# Revit family: Lighting-UrbanSystem-GEWISS-URBAN[O3]-LED-SIDE_COUPLING_OPTIC_STREET
name_source: partatom
category: Apparecchi per illuminazione
units: mm (PartAtom-declared; Revit-internal decimal feet)

## family parameters
Condiviso = No
Host = Superficie
Numero OmniClass = 23.80.70.00
Punto di calcolo locali = Sì
Quota connettore circolare = Usa diametro
Sorgente d'illuminazione = No
Taglio con vuoti quando caricato = No
Tipo di parte = Normale
Titolo OmniClass = Lighting

## types (4) — shared parameters
Application = External
Catalogue = LIGHTING
Catalogue Range = URBAN [O3]
Colour = Graphite grey
Colour temperature = 4000 K (CRI 70)
Colour temperature: = 4000 K (CRI 70)
Driver type = Constant Current Driver Led
Electrocod = 244C
Finitura = GEWISS - GRIGIO GRAFITE
IDF = 77868679-f757-4753-85ef-7763ddad7a87
IDT = 85d5c301-9efa-429f-8169-5776374b703b
IP degree = IP66
Immagine tipo = GW87601.jpg
Insulation class = II
LED Life time (L80B10) = 100000H
LED Life time (L90B20) = 50000H
LED LifeTime (L80B20) = 50000H
LED current = 530mA
Maximum surface exposed to the wind = 0,25M2
Minimum distance from the illuminated object = 1M
Operating temperature: = -25 +35 °C
Optic = Street - ULOR: 0%
Photobiologic Risk = RG1/RG2 @ 20cm
Pilot current = 530mA
Produttore = GEWISS S.p.A.
Prospetto di default = 1219 mm
Risk photobiological = RG1/RG2 @ 20cm
SEO = Street lighting
Shock resistance = IK08 BODY - IK06 LENS
Suitable for = Commercial side brackets with side connection
Suitable for: = Commercial side brackets with side connection
Technical sheet = https://www.gewiss.com
Type of lamp: = LED
Type of light source = LED
URL = https://www.gewiss.com
Version file RFA = 20.11
Vetro = GEWISS - VETRO
Voltage: = 220/240 V - 50/60 Hz
Warranty = 5 years
Working temperature = -25 +35 °C

## per-type parameters (varying)
| type | Descrizione | EAN code | Lumen output (lm) | Modello | No. Chorus modules | Nominal flux (lm) | Number of modules | Power supply operation | System power | Type | Typology | Voltage | Weight (kg) | Weight (kg): |
| GW87608 - URBAN LED 4M 4000K STR. SIDE B. GRA.GR. | URBAN LED 4M 4000K STR. SIDE B. GRA.GR. | 8011564786165 | 11240 | GW87608 | 4 (4x16 LED) | 13400 | 4 (4x16 LED) |  | 105W | Stand alone | Stand alone | 220/240 V - 50/60 Hz - Stand alone and/or possibility of dimmer 1-10 V | 11 | 11 |
| GW87607 - URBAN LED 3M 4000K STR. SIDE B. GRA.GR. | URBAN LED 3M 4000K STR. SIDE B. GRA.GR. | 8011564786158 | 8590 | GW87607 | 3 (3x16 LED) | 10230 | 3 (3x16 LED) |  | 81W | Stand alone | Stand alone | 220/240 V - 50/60 Hz - Stand alone and/or possibility of dimmer 1-10 V | 10,3 | 10,3 |
| GW87628 - URBAN LED 4M 4000K BI.STR.SIDE B.GRA.GR. | URBAN LED 4M 4000K BI.STR.SIDE B.GRA.GR. | 8011564786233 | 11240 | GW87628 | 4 (4x16 LED) | 13400 | 4 (4x16 LED) | Bi power | 105W |  |  | 220/240 V - 50/60 Hz - Bi-power with self-learning | 11 | 11 |
| GW87627 - URBAN LED 3M 4000K BI.STR.SIDE B.GRA.GR. | URBAN LED 3M 4000K BI.STR.SIDE B.GRA.GR. | 8011564786226 | 8590 | GW87627 | 3 (3x16 LED) | 10230 | 3 (3x16 LED) | Bi power | 81W |  |  | 220/240 V - 50/60 Hz - Bi-power with self-learning | 10,3 | 10,3 |

## geometry (parser evidence)
native form markers: Blend x4
no freeform markers — native parametric forms only
